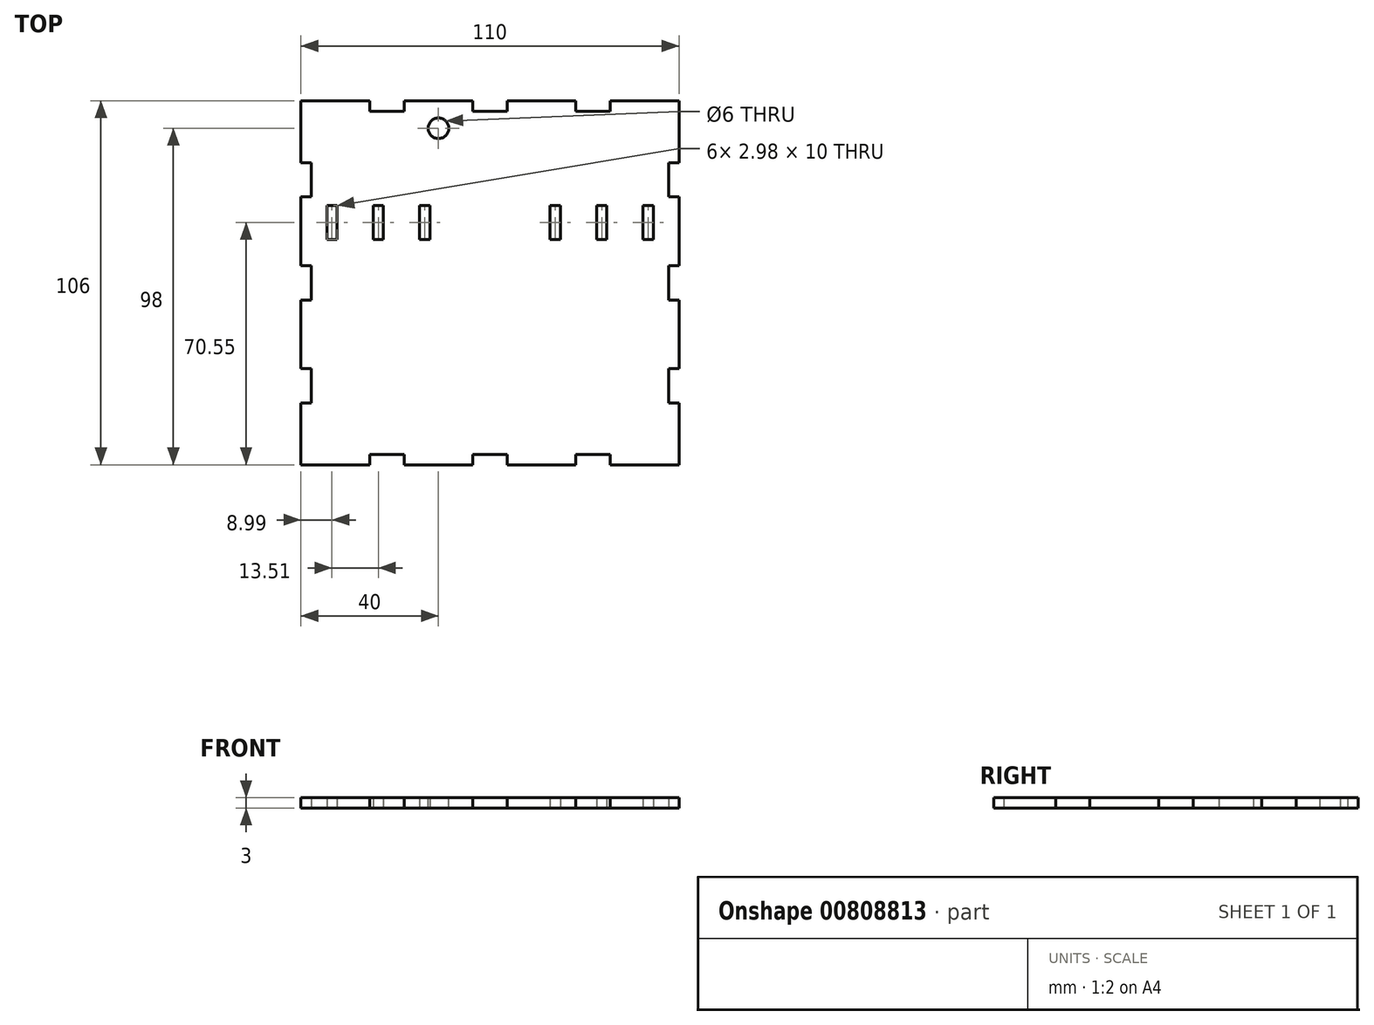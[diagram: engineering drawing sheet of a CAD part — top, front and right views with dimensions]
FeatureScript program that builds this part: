
annotation { "Feature Type Name" : "Feature", "Feature Type Description" : "" }
export const myFeature = defineFeature(function(context is Context, id is Id, definition is map)
    precondition{}
    {
        {
            var Q0;
            Q0=qCreatedBy(makeId("Top.planeOp"),FACE);
            var sketch = newSketch(context, id + "F0", { "sketchPlane" : qUnion([Q0])});
            skLineSegment(sketch, "E0.bottom", {"start": v(55, -53) * mm, "end": v(-55, -53) * mm});
            skLineSegment(sketch, "E0.top", {"start": v(55, 53) * mm, "end": v(-55, 53) * mm});
            skLineSegment(sketch, "E0.left", {"start": v(55, -53) * mm, "end": v(55, 53) * mm});
            skLineSegment(sketch, "E0.right", {"start": v(-55, -53) * mm, "end": v(-55, 53) * mm});
            skPoint(sketch, "E0.middle", {"position": v(0, 0) * mm});
            skLineSegment(sketch, "E1.bottom", {"start": v(-52, -5) * mm, "end": v(-58, -5) * mm});
            skLineSegment(sketch, "E1.top", {"start": v(-52, 5) * mm, "end": v(-58, 5) * mm});
            skLineSegment(sketch, "E1.left", {"start": v(-52, -5) * mm, "end": v(-52, 5) * mm});
            skLineSegment(sketch, "E1.right", {"start": v(-58, -5) * mm, "end": v(-58, 5) * mm});
            skPoint(sketch, "E1.middle", {"position": v(-55, 0) * mm});
            skLineSegment(sketch, "E2.bottom", {"start": v(-52, -25) * mm, "end": v(-58, -25) * mm});
            skLineSegment(sketch, "E2.top", {"start": v(-52, -35) * mm, "end": v(-58, -35) * mm});
            skLineSegment(sketch, "E2.left", {"start": v(-52, -25) * mm, "end": v(-52, -35) * mm});
            skLineSegment(sketch, "E2.right", {"start": v(-58, -25) * mm, "end": v(-58, -35) * mm});
            skPoint(sketch, "E2.middle", {"position": v(-55, -30) * mm});
            skLineSegment(sketch, "E3.bottom", {"start": v(-52, 35) * mm, "end": v(-58, 35) * mm});
            skLineSegment(sketch, "E3.top", {"start": v(-52, 25) * mm, "end": v(-58, 25) * mm});
            skLineSegment(sketch, "E3.left", {"start": v(-52, 35) * mm, "end": v(-52, 25) * mm});
            skLineSegment(sketch, "E3.right", {"start": v(-58, 35) * mm, "end": v(-58, 25) * mm});
            skPoint(sketch, "E3.middle", {"position": v(-55, 30) * mm});
            skLineSegment(sketch, "E4.bottom", {"start": v(5, -50) * mm, "end": v(-5, -50) * mm});
            skLineSegment(sketch, "E4.top", {"start": v(5, -56) * mm, "end": v(-5, -56) * mm});
            skLineSegment(sketch, "E4.left", {"start": v(5, -50) * mm, "end": v(5, -56) * mm});
            skLineSegment(sketch, "E4.right", {"start": v(-5, -50) * mm, "end": v(-5, -56) * mm});
            skPoint(sketch, "E4.middle", {"position": v(0, -53) * mm});
            skLineSegment(sketch, "E5.bottom", {"start": v(35, -50) * mm, "end": v(25, -50) * mm});
            skLineSegment(sketch, "E5.top", {"start": v(35, -56) * mm, "end": v(25, -56) * mm});
            skLineSegment(sketch, "E5.left", {"start": v(35, -50) * mm, "end": v(35, -56) * mm});
            skLineSegment(sketch, "E5.right", {"start": v(25, -50) * mm, "end": v(25, -56) * mm});
            skPoint(sketch, "E5.middle", {"position": v(30, -53) * mm});
            skLineSegment(sketch, "E6.bottom", {"start": v(-25, -50) * mm, "end": v(-35, -50) * mm});
            skLineSegment(sketch, "E6.top", {"start": v(-25, -56) * mm, "end": v(-35, -56) * mm});
            skLineSegment(sketch, "E6.left", {"start": v(-25, -50) * mm, "end": v(-25, -56) * mm});
            skLineSegment(sketch, "E6.right", {"start": v(-35, -50) * mm, "end": v(-35, -56) * mm});
            skPoint(sketch, "E6.middle", {"position": v(-30, -53) * mm});
            skLineSegment(sketch, "E7.1.0", {"start": v(25, -52) * mm, "end": v(35, -52) * mm});
            skLineSegment(sketch, "E7.1.1", {"start": v(35, -52) * mm, "end": v(35, -58) * mm});
            skLineSegment(sketch, "E7.1.2", {"start": v(25, -58) * mm, "end": v(35, -58) * mm});
            skLineSegment(sketch, "E7.1.3", {"start": v(25, -52) * mm, "end": v(25, -58) * mm});
            skLineSegment(sketch, "E7.1.4", {"start": v(5, -52) * mm, "end": v(5, -58) * mm});
            skLineSegment(sketch, "E7.1.5", {"start": v(5, -52) * mm, "end": v(-5, -52) * mm});
            skLineSegment(sketch, "E7.1.6", {"start": v(-5, -52) * mm, "end": v(-5, -58) * mm});
            skLineSegment(sketch, "E7.1.7", {"start": v(5, -58) * mm, "end": v(-5, -58) * mm});
            skLineSegment(sketch, "E7.1.8", {"start": v(-25, -52) * mm, "end": v(-25, -58) * mm});
            skLineSegment(sketch, "E7.1.9", {"start": v(-35, -52) * mm, "end": v(-25, -52) * mm});
            skLineSegment(sketch, "E7.1.10", {"start": v(-35, -52) * mm, "end": v(-35, -58) * mm});
            skLineSegment(sketch, "E7.1.11", {"start": v(-35, -58) * mm, "end": v(-25, -58) * mm});
            skLineSegment(sketch, "E7.1.13", {"start": v(50, -25) * mm, "end": v(56, -25) * mm});
            skLineSegment(sketch, "E7.1.14", {"start": v(56, -25) * mm, "end": v(56, -35) * mm});
            skLineSegment(sketch, "E7.1.15", {"start": v(50, -35) * mm, "end": v(56, -35) * mm});
            skLineSegment(sketch, "E7.1.16", {"start": v(50, -5) * mm, "end": v(56, -5) * mm});
            skLineSegment(sketch, "E7.1.17", {"start": v(56, 5) * mm, "end": v(56, -5) * mm});
            skLineSegment(sketch, "E7.1.19", {"start": v(50, 5) * mm, "end": v(56, 5) * mm});
            skLineSegment(sketch, "E7.1.20", {"start": v(50, 25) * mm, "end": v(56, 25) * mm});
            skLineSegment(sketch, "E7.1.21", {"start": v(50, 35) * mm, "end": v(56, 35) * mm});
            skLineSegment(sketch, "E7.1.22", {"start": v(56, 35) * mm, "end": v(56, 25) * mm});
            skLineSegment(sketch, "E7.2.0", {"start": v(52, 25) * mm, "end": v(52, 35) * mm});
            skLineSegment(sketch, "E7.2.1", {"start": v(52, 35) * mm, "end": v(58, 35) * mm});
            skLineSegment(sketch, "E7.2.2", {"start": v(58, 25) * mm, "end": v(58, 35) * mm});
            skLineSegment(sketch, "E7.2.3", {"start": v(52, 25) * mm, "end": v(58, 25) * mm});
            skLineSegment(sketch, "E7.2.4", {"start": v(52, 5) * mm, "end": v(58, 5) * mm});
            skLineSegment(sketch, "E7.2.5", {"start": v(52, 5) * mm, "end": v(52, -5) * mm});
            skLineSegment(sketch, "E7.2.6", {"start": v(52, -5) * mm, "end": v(58, -5) * mm});
            skLineSegment(sketch, "E7.2.7", {"start": v(58, 5) * mm, "end": v(58, -5) * mm});
            skLineSegment(sketch, "E7.2.8", {"start": v(52, -25) * mm, "end": v(58, -25) * mm});
            skLineSegment(sketch, "E7.2.9", {"start": v(52, -35) * mm, "end": v(52, -25) * mm});
            skLineSegment(sketch, "E7.2.10", {"start": v(52, -35) * mm, "end": v(58, -35) * mm});
            skLineSegment(sketch, "E7.2.11", {"start": v(58, -35) * mm, "end": v(58, -25) * mm});
            skLineSegment(sketch, "E7.2.12", {"start": v(25, 50) * mm, "end": v(35, 50) * mm});
            skLineSegment(sketch, "E7.2.13", {"start": v(25, 50) * mm, "end": v(25, 56) * mm});
            skLineSegment(sketch, "E7.2.14", {"start": v(25, 56) * mm, "end": v(35, 56) * mm});
            skLineSegment(sketch, "E7.2.15", {"start": v(35, 50) * mm, "end": v(35, 56) * mm});
            skLineSegment(sketch, "E7.2.16", {"start": v(5, 50) * mm, "end": v(5, 56) * mm});
            skLineSegment(sketch, "E7.2.17", {"start": v(-5, 56) * mm, "end": v(5, 56) * mm});
            skLineSegment(sketch, "E7.2.18", {"start": v(-5, 50) * mm, "end": v(5, 50) * mm});
            skLineSegment(sketch, "E7.2.19", {"start": v(-5, 50) * mm, "end": v(-5, 56) * mm});
            skLineSegment(sketch, "E7.2.20", {"start": v(-25, 50) * mm, "end": v(-25, 56) * mm});
            skLineSegment(sketch, "E7.2.21", {"start": v(-35, 50) * mm, "end": v(-35, 56) * mm});
            skLineSegment(sketch, "E7.2.22", {"start": v(-35, 56) * mm, "end": v(-25, 56) * mm});
            skLineSegment(sketch, "E7.2.23", {"start": v(-35, 50) * mm, "end": v(-25, 50) * mm});
            skLineSegment(sketch, "E7.3.0", {"start": v(-25, 52) * mm, "end": v(-35, 52) * mm});
            skLineSegment(sketch, "E7.3.1", {"start": v(-35, 52) * mm, "end": v(-35, 58) * mm});
            skLineSegment(sketch, "E7.3.2", {"start": v(-25, 58) * mm, "end": v(-35, 58) * mm});
            skLineSegment(sketch, "E7.3.3", {"start": v(-25, 52) * mm, "end": v(-25, 58) * mm});
            skLineSegment(sketch, "E7.3.4", {"start": v(-5, 52) * mm, "end": v(-5, 58) * mm});
            skLineSegment(sketch, "E7.3.5", {"start": v(-5, 52) * mm, "end": v(5, 52) * mm});
            skLineSegment(sketch, "E7.3.6", {"start": v(5, 52) * mm, "end": v(5, 58) * mm});
            skLineSegment(sketch, "E7.3.7", {"start": v(-5, 58) * mm, "end": v(5, 58) * mm});
            skLineSegment(sketch, "E7.3.8", {"start": v(25, 52) * mm, "end": v(25, 58) * mm});
            skLineSegment(sketch, "E7.3.9", {"start": v(35, 52) * mm, "end": v(25, 52) * mm});
            skLineSegment(sketch, "E7.3.10", {"start": v(35, 52) * mm, "end": v(35, 58) * mm});
            skLineSegment(sketch, "E7.3.11", {"start": v(35, 58) * mm, "end": v(25, 58) * mm});
            skLineSegment(sketch, "E7.3.13", {"start": v(-50, 25) * mm, "end": v(-56, 25) * mm});
            skLineSegment(sketch, "E7.3.14", {"start": v(-56, 25) * mm, "end": v(-56, 35) * mm});
            skLineSegment(sketch, "E7.3.15", {"start": v(-50, 35) * mm, "end": v(-56, 35) * mm});
            skLineSegment(sketch, "E7.3.16", {"start": v(-50, 5) * mm, "end": v(-56, 5) * mm});
            skLineSegment(sketch, "E7.3.17", {"start": v(-56, -5) * mm, "end": v(-56, 5) * mm});
            skLineSegment(sketch, "E7.3.19", {"start": v(-50, -5) * mm, "end": v(-56, -5) * mm});
            skLineSegment(sketch, "E7.3.20", {"start": v(-50, -25) * mm, "end": v(-56, -25) * mm});
            skLineSegment(sketch, "E7.3.21", {"start": v(-50, -35) * mm, "end": v(-56, -35) * mm});
            skLineSegment(sketch, "E7.3.22", {"start": v(-56, -35) * mm, "end": v(-56, -25) * mm});
            skSolve(sketch);
        }
        {
            var Q0;
            {var subQ0=sQuery(id+"F0.wireOp",EDGE,"E6.bottom");Q0=makeQuery(id+"F0.imprint","IMPRINT",FACE,{"disambiguationData":[TD([[makeQuery(id+"F0.imprint","IMPRINT",EDGE,{"derivedFrom":subQ0}),-1.0]])]});}
            var Q1;
            {var subQ0=sQuery(id+"F0.wireOp",EDGE,"E4.bottom");Q1=makeQuery(id+"F0.imprint","IMPRINT",FACE,{"disambiguationData":[TD([[makeQuery(id+"F0.imprint","IMPRINT",EDGE,{"derivedFrom":subQ0}),-1.0]])]});}
            var Q2;
            {var subQ0=sQuery(id+"F0.wireOp",EDGE,"E5.bottom");Q2=makeQuery(id+"F0.imprint","IMPRINT",FACE,{"disambiguationData":[TD([[makeQuery(id+"F0.imprint","IMPRINT",EDGE,{"derivedFrom":subQ0}),-1.0]])]});}
            var Q3;
            {var subQ0=sQuery(id+"F0.wireOp",EDGE,"E7.2.18");Q3=makeQuery(id+"F0.imprint","IMPRINT",FACE,{"disambiguationData":[TD([[makeQuery(id+"F0.imprint","IMPRINT",EDGE,{"derivedFrom":subQ0}),-1.0]])]});}
            var Q4;
            {var subQ0=sQuery(id+"F0.wireOp",EDGE,"E7.2.23");Q4=makeQuery(id+"F0.imprint","IMPRINT",FACE,{"disambiguationData":[TD([[makeQuery(id+"F0.imprint","IMPRINT",EDGE,{"derivedFrom":subQ0}),-1.0]])]});}
            var Q5;
            {var subQ0=sQuery(id+"F0.wireOp",EDGE,"E7.2.12");Q5=makeQuery(id+"F0.imprint","IMPRINT",FACE,{"disambiguationData":[TD([[makeQuery(id+"F0.imprint","IMPRINT",EDGE,{"derivedFrom":subQ0}),-1.0]])]});}
            extrude(context, id + "F1", {"entities" : qUnion([Q0, Q1, Q2, Q3, Q4, Q5]), "depth" : 3 * mm, "offsetDistance" : 25 * mm});
        }
        {
            var Q0;
            Q0=makeQuery(id+"F1.opExtrude","CAP_FACE",FACE,{"disambiguationData":[OSD([sQuery(id+"F0.wireOp",EDGE,"E0.bottom"),sQuery(id+"F0.wireOp",EDGE,"E0.top"),sQuery(id+"F0.wireOp",EDGE,"E0.left"),sQuery(id+"F0.wireOp",EDGE,"E0.right"),sQuery(id+"F0.wireOp",EDGE,"E7.1.0"),sQuery(id+"F0.wireOp",EDGE,"E7.1.1"),sQuery(id+"F0.wireOp",EDGE,"E7.1.3"),sQuery(id+"F0.wireOp",EDGE,"E7.1.4"),sQuery(id+"F0.wireOp",EDGE,"E7.1.5"),sQuery(id+"F0.wireOp",EDGE,"E7.1.6"),sQuery(id+"F0.wireOp",EDGE,"E7.1.8"),sQuery(id+"F0.wireOp",EDGE,"E7.1.9"),sQuery(id+"F0.wireOp",EDGE,"E7.1.10"),sQuery(id+"F0.wireOp",EDGE,"E7.2.0"),sQuery(id+"F0.wireOp",EDGE,"E7.2.1"),sQuery(id+"F0.wireOp",EDGE,"E7.2.3"),sQuery(id+"F0.wireOp",EDGE,"E7.2.4"),sQuery(id+"F0.wireOp",EDGE,"E7.2.5"),sQuery(id+"F0.wireOp",EDGE,"E7.2.6"),sQuery(id+"F0.wireOp",EDGE,"E7.2.8"),sQuery(id+"F0.wireOp",EDGE,"E7.2.9"),sQuery(id+"F0.wireOp",EDGE,"E7.2.10"),sQuery(id+"F0.wireOp",EDGE,"E7.3.0"),sQuery(id+"F0.wireOp",EDGE,"E7.3.1"),sQuery(id+"F0.wireOp",EDGE,"E7.3.3"),sQuery(id+"F0.wireOp",EDGE,"E7.3.4"),sQuery(id+"F0.wireOp",EDGE,"E7.3.5"),sQuery(id+"F0.wireOp",EDGE,"E7.3.6"),sQuery(id+"F0.wireOp",EDGE,"E7.3.8"),sQuery(id+"F0.wireOp",EDGE,"E7.3.9"),sQuery(id+"F0.wireOp",EDGE,"E7.3.10"),sQuery(id+"F0.wireOp",EDGE,"E7.3.12"),sQuery(id+"F0.wireOp",EDGE,"E7.3.13"),sQuery(id+"F0.wireOp",EDGE,"E7.3.15"),sQuery(id+"F0.wireOp",EDGE,"E7.3.16"),sQuery(id+"F0.wireOp",EDGE,"E7.3.18"),sQuery(id+"F0.wireOp",EDGE,"E7.3.19"),sQuery(id+"F0.wireOp",EDGE,"E7.3.20"),sQuery(id+"F0.wireOp",EDGE,"E7.3.21"),sQuery(id+"F0.wireOp",EDGE,"E7.3.23")])],"isStart":true});
            var sketch = newSketch(context, id + "F2", { "sketchPlane" : qUnion([Q0])});
            skLineSegment(sketch, "E8.bottom", {"start": v(-44.52, -12.55) * mm, "end": v(-47.5, -12.55) * mm});
            skLineSegment(sketch, "E8.top", {"start": v(-44.52, -22.55) * mm, "end": v(-47.5, -22.55) * mm});
            skLineSegment(sketch, "E8.left", {"start": v(-44.52, -12.55) * mm, "end": v(-44.52, -22.55) * mm});
            skLineSegment(sketch, "E8.right", {"start": v(-47.5, -12.55) * mm, "end": v(-47.5, -22.55) * mm});
            skPoint(sketch, "E8.middle", {"position": v(-46.01, -17.55) * mm});
            skLineSegment(sketch, "E9.bottom", {"start": v(-31.01, -12.55) * mm, "end": v(-34, -12.55) * mm});
            skLineSegment(sketch, "E9.top", {"start": v(-31.01, -22.55) * mm, "end": v(-34, -22.55) * mm});
            skLineSegment(sketch, "E9.left", {"start": v(-31.01, -12.55) * mm, "end": v(-31.01, -22.55) * mm});
            skLineSegment(sketch, "E9.right", {"start": v(-34, -12.55) * mm, "end": v(-34, -22.55) * mm});
            skPoint(sketch, "E9.middle", {"position": v(-32.5, -17.55) * mm});
            skLineSegment(sketch, "E10.bottom", {"start": v(-17.5, -12.55) * mm, "end": v(-20.48, -12.55) * mm});
            skLineSegment(sketch, "E10.top", {"start": v(-17.5, -22.55) * mm, "end": v(-20.48, -22.55) * mm});
            skLineSegment(sketch, "E10.left", {"start": v(-17.5, -12.55) * mm, "end": v(-17.5, -22.55) * mm});
            skLineSegment(sketch, "E10.right", {"start": v(-20.48, -12.55) * mm, "end": v(-20.48, -22.55) * mm});
            skPoint(sketch, "E10.middle", {"position": v(-19, -17.55) * mm});
            skLineSegment(sketch, "E11", {"start": v(-55, -35) * mm, "end": v(-58, -35) * mm});
            skLineSegment(sketch, "E12", {"start": v(0, -50) * mm, "end": v(0, -41.83) * mm});
            skLineSegment(sketch, "E13.MirrorCS", {"start": v(17.5, -12.55) * mm, "end": v(17.5, -22.55) * mm});
            skLineSegment(sketch, "E14.MirrorCS", {"start": v(17.5, -22.55) * mm, "end": v(20.48, -22.55) * mm});
            skLineSegment(sketch, "E15.MirrorCS", {"start": v(20.48, -12.55) * mm, "end": v(20.48, -22.55) * mm});
            skLineSegment(sketch, "E16.MirrorCS", {"start": v(17.5, -12.55) * mm, "end": v(20.48, -12.55) * mm});
            skLineSegment(sketch, "E17.MirrorCS", {"start": v(31.01, -12.55) * mm, "end": v(31.01, -22.55) * mm});
            skLineSegment(sketch, "E18.MirrorCS", {"start": v(31.01, -22.55) * mm, "end": v(34, -22.55) * mm});
            skLineSegment(sketch, "E19.MirrorCS", {"start": v(34, -12.55) * mm, "end": v(34, -22.55) * mm});
            skLineSegment(sketch, "E20.MirrorCS", {"start": v(31.01, -12.55) * mm, "end": v(34, -12.55) * mm});
            skLineSegment(sketch, "E21.MirrorCS", {"start": v(44.52, -12.55) * mm, "end": v(44.52, -22.55) * mm});
            skLineSegment(sketch, "E22.MirrorCS", {"start": v(44.52, -22.55) * mm, "end": v(47.5, -22.55) * mm});
            skLineSegment(sketch, "E23.MirrorCS", {"start": v(47.5, -12.55) * mm, "end": v(47.5, -22.55) * mm});
            skLineSegment(sketch, "E24.MirrorCS", {"start": v(44.52, -12.55) * mm, "end": v(47.5, -12.55) * mm});
            skLineSegment(sketch, "E25.top", {"start": v(-50, 50) * mm, "end": v(50, 50) * mm});
            skLineSegment(sketch, "E25.left", {"start": v(-50, -50) * mm, "end": v(-50, 50) * mm});
            skPoint(sketch, "E25.middle", {"position": v(0, 0) * mm});
            skSolve(sketch);
        }
        {
            var Q0;
            Q0=qSketchRegion(id+"F2",true);
            extrude(context, id + "F3", {"entities" : qUnion([Q0]), "operationType" : NewBodyOperationType.REMOVE, "oppositeDirection" : true, "depth" : 25 * mm, "offsetDistance" : 25 * mm});
        }
        {
            var Q0;
            Q0=makeQuery(id+"F1.opExtrude","CAP_FACE",FACE,{"disambiguationData":[OSD([sQuery(id+"F0.wireOp",EDGE,"E0.bottom"),sQuery(id+"F0.wireOp",EDGE,"E0.top"),sQuery(id+"F0.wireOp",EDGE,"E0.left"),sQuery(id+"F0.wireOp",EDGE,"E0.right"),sQuery(id+"F0.wireOp",EDGE,"E1.bottom"),sQuery(id+"F0.wireOp",EDGE,"E1.top"),sQuery(id+"F0.wireOp",EDGE,"E1.left"),sQuery(id+"F0.wireOp",EDGE,"E2.bottom"),sQuery(id+"F0.wireOp",EDGE,"E2.top"),sQuery(id+"F0.wireOp",EDGE,"E2.left"),sQuery(id+"F0.wireOp",EDGE,"E3.bottom"),sQuery(id+"F0.wireOp",EDGE,"E3.top"),sQuery(id+"F0.wireOp",EDGE,"E3.left"),sQuery(id+"F0.wireOp",EDGE,"E4.bottom"),sQuery(id+"F0.wireOp",EDGE,"E5.bottom"),sQuery(id+"F0.wireOp",EDGE,"E6.bottom"),sQuery(id+"F0.wireOp",EDGE,"E7.1.1"),sQuery(id+"F0.wireOp",EDGE,"E7.1.3"),sQuery(id+"F0.wireOp",EDGE,"E7.1.4"),sQuery(id+"F0.wireOp",EDGE,"E7.1.6"),sQuery(id+"F0.wireOp",EDGE,"E7.1.8"),sQuery(id+"F0.wireOp",EDGE,"E7.1.10"),sQuery(id+"F0.wireOp",EDGE,"E7.2.0"),sQuery(id+"F0.wireOp",EDGE,"E7.2.1"),sQuery(id+"F0.wireOp",EDGE,"E7.2.3"),sQuery(id+"F0.wireOp",EDGE,"E7.2.4"),sQuery(id+"F0.wireOp",EDGE,"E7.2.5"),sQuery(id+"F0.wireOp",EDGE,"E7.2.6"),sQuery(id+"F0.wireOp",EDGE,"E7.2.8"),sQuery(id+"F0.wireOp",EDGE,"E7.2.9"),sQuery(id+"F0.wireOp",EDGE,"E7.2.10"),sQuery(id+"F0.wireOp",EDGE,"E7.2.12"),sQuery(id+"F0.wireOp",EDGE,"E7.2.18"),sQuery(id+"F0.wireOp",EDGE,"E7.2.23"),sQuery(id+"F0.wireOp",EDGE,"E7.3.1"),sQuery(id+"F0.wireOp",EDGE,"E7.3.3"),sQuery(id+"F0.wireOp",EDGE,"E7.3.4"),sQuery(id+"F0.wireOp",EDGE,"E7.3.6"),sQuery(id+"F0.wireOp",EDGE,"E7.3.8"),sQuery(id+"F0.wireOp",EDGE,"E7.3.10")])],"isStart":false});
            var sketch = newSketch(context, id + "F4", { "sketchPlane" : qUnion([Q0])});
            skLineSegment(sketch, "E26.bottom", {"start": v(-50, 50) * mm, "end": v(50, 50) * mm});
            skLineSegment(sketch, "E26.top", {"start": v(-50, -50) * mm, "end": v(50, -50) * mm});
            skLineSegment(sketch, "E26.left", {"start": v(-50, 50) * mm, "end": v(-50, -50) * mm});
            skLineSegment(sketch, "E26.right", {"start": v(50, 50) * mm, "end": v(50, -50) * mm});
            skPoint(sketch, "E26.middle", {"position": v(0, 0) * mm});
            skCircle(sketch, "E27", {"center": v(-15, 45) * mm, "radius": 3 * mm});
            skSolve(sketch);
        }
        {
            var Q0;
            Q0=makeQuery(id+"F4.imprint","IMPRINT",FACE,{"disambiguationData":[TD([[makeQuery(id+"F4.imprint","IMPRINT",EDGE,{"derivedFrom":sQuery(id+"F4.wireOp",EDGE,"E27")}),1.0]])]});
            extrude(context, id + "F5", {"entities" : qUnion([Q0]), "operationType" : NewBodyOperationType.REMOVE, "oppositeDirection" : true, "depth" : 25 * mm, "offsetDistance" : 25 * mm});
        }
    });
